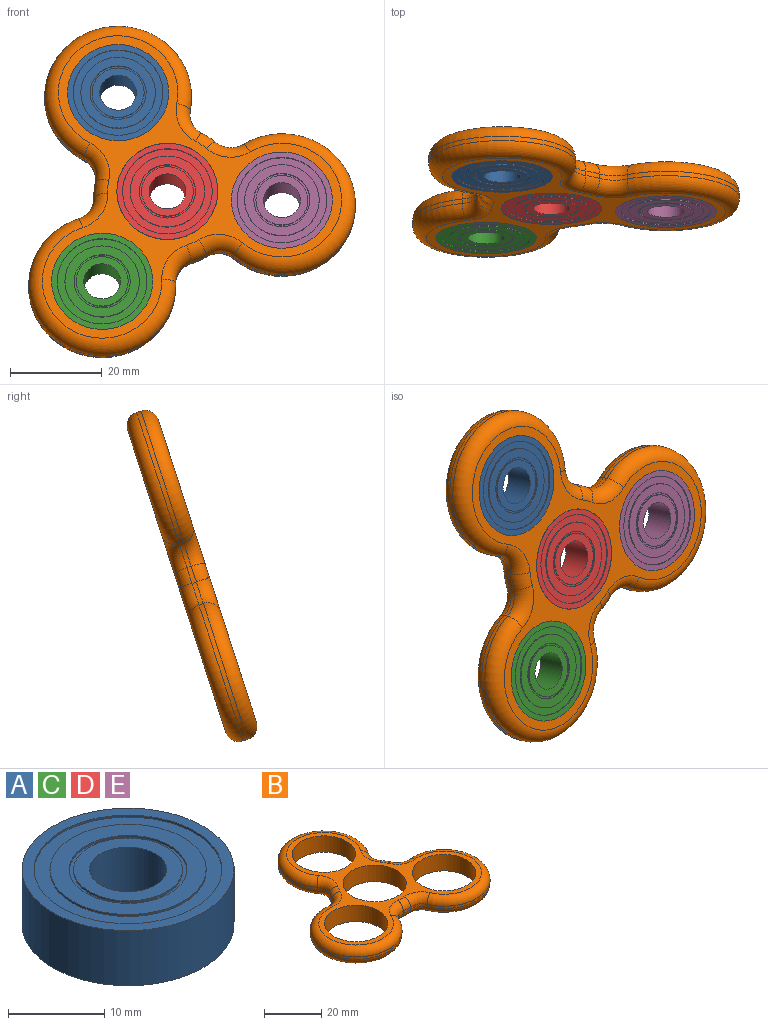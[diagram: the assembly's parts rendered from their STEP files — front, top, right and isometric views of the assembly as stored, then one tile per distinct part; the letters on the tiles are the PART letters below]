
ASSEMBLY  parts=5 mates=4
PART A: 20 faces, bbox 22x22x7 mm
  f0: plane 11.3x11.3mm, normal (0,0,-1), area 50mm2, adj f2,f8
  f1: cylinder r=11mm len=22mm, axis (0,0,-1), area 483.8mm2, adj f3,f12
  f2: cylinder r=4mm len=8mm, axis (0,0,-1), area 175.9mm2, adj f0,f11
  f3: plane 22x22mm, normal (0,0,-1), area 81.5mm2, adj f1,f5
  f4: cylinder r=8.1mm len=16.2mm, axis (0,0,-1), area 12.7mm2, adj f6,f7
  f5: cylinder r=9.75mm len=19.5mm, axis (0,0,-1), area 15.3mm2, adj f3,f6
  f6: plane 19.5x19.5mm, normal (0,0,-1), area 92.5mm2, adj f4,f5
  f7: plane 16.2x16.2mm, normal (0,0,-1), area 89.2mm2, adj f4,f9
  f8: cylinder r=5.65mm len=11.3mm, axis (0,0,-1), area 8.9mm2, adj f0,f10
  f9: cylinder r=6.1mm len=12.2mm, axis (0,0,-1), area 9.6mm2, adj f7,f10
  f10: plane 12.2x12.2mm, normal (0,0,-1), area 16.6mm2, adj f8,f9
  f11: plane 11.3x11.3mm, normal (0,0,1), area 50mm2, adj f2,f17
  f12: plane 22x22mm, normal (0,0,1), area 81.5mm2, adj f1,f14
  f13: cylinder r=8.1mm len=16.2mm, axis (0,0,1), area 12.7mm2, adj f15,f16
  f14: cylinder r=9.75mm len=19.5mm, axis (0,0,1), area 15.3mm2, adj f12,f15
  f15: plane 19.5x19.5mm, normal (0,0,1), area 92.5mm2, adj f13,f14
  f16: plane 16.2x16.2mm, normal (0,0,1), area 89.2mm2, adj f13,f18
  f17: cylinder r=5.65mm len=11.3mm, axis (0,0,1), area 8.9mm2, adj f11,f19
  f18: cylinder r=6.1mm len=12.2mm, axis (0,0,1), area 9.6mm2, adj f16,f19
  f19: plane 12.2x12.2mm, normal (0,0,1), area 16.6mm2, adj f17,f18
PART B: 42 faces, bbox 77.9x72.1x7 mm
  f0: plane 69.3x63.5mm, normal (0,0,-1), area 677.7mm2, adj f4,f6,f9,f11,f18,f19,f20,f21
  f1: cylinder r=16mm len=3.64mm, axis (0,0,-1), area 3.6mm2, adj f12,f15,f21,f34
  f2: cylinder r=16mm len=3.15mm, axis (0,0,-1), area 3.6mm2, adj f13,f16,f29,f33
  f3: cylinder r=16mm len=3.15mm, axis (0,0,-1), area 3.6mm2, adj f14,f17,f22,f41
  f4: cylinder r=11mm len=22mm, axis (0,0,-1), area 483.8mm2, adj f0,f5
  f5: plane 69.3x63.5mm, normal (0,0,1), area 677.7mm2, adj f4,f6,f9,f11,f30,f31,f32,f33
  f6: cylinder r=11mm len=22mm, axis (0,0,-1), area 483.8mm2, adj f0,f5
  f7: cylinder r=16mm len=32mm, axis (0,0,-1), area 70.7mm2, adj f16,f17,f26,f37
  f8: cylinder r=16mm len=32mm, axis (0,0,-1), area 70.7mm2, adj f14,f15,f18,f38
  f9: cylinder r=11mm len=22mm, axis (0,0,-1), area 483.8mm2, adj f0,f5
  f10: cylinder r=16mm len=32mm, axis (0,0,-1), area 70.7mm2, adj f12,f13,f25,f30
  f11: cylinder r=11mm len=22mm, axis (0,0,-1), area 483.8mm2, adj f0,f5
  f12: cylinder r=5mm len=5.16mm, axis (0,0,1), area 6.4mm2, adj f1,f10,f23,f32
  f13: cylinder r=5mm len=5.16mm, axis (0,0,-1), area 6.4mm2, adj f2,f10,f27,f31
  f14: cylinder r=5mm len=5.16mm, axis (0,0,1), area 6.4mm2, adj f3,f8,f20,f40
  f15: cylinder r=5mm len=5.16mm, axis (0,0,-1), area 6.4mm2, adj f1,f8,f19,f36
  f16: cylinder r=5mm len=5.95mm, axis (0,0,1), area 6.4mm2, adj f2,f7,f28,f35
  f17: cylinder r=5mm len=5.95mm, axis (0,0,-1), area 6.4mm2, adj f3,f7,f24,f39
  f18: torus R=13mm, axis (0,0,-1), area 310.3mm2, adj f0,f8,f19,f20
  f19: torus R=8mm, axis (0,0,-1), area 36.6mm2, adj f0,f15,f18,f21
  f20: torus R=8mm, axis (0,0,-1), area 36.6mm2, adj f0,f14,f18,f22
  f21: torus R=13mm, axis (0,0,-1), area 16mm2, adj f0,f1,f19,f23
  f22: torus R=13mm, axis (0,0,-1), area 16mm2, adj f0,f3,f20,f24
  f23: torus R=8mm, axis (0,0,-1), area 36.6mm2, adj f0,f12,f21,f25
  f24: torus R=8mm, axis (0,0,-1), area 36.6mm2, adj f0,f17,f22,f26
  f25: torus R=13mm, axis (0,0,-1), area 310.3mm2, adj f0,f10,f23,f27
  f26: torus R=13mm, axis (0,0,-1), area 310.3mm2, adj f0,f7,f24,f28
  f27: torus R=8mm, axis (0,0,-1), area 36.6mm2, adj f0,f13,f25,f29
  f28: torus R=8mm, axis (0,0,-1), area 36.6mm2, adj f0,f16,f26,f29
  f29: torus R=13mm, axis (0,0,-1), area 16mm2, adj f0,f2,f27,f28
  f30: torus R=13mm, axis (0,0,-1), area 310.3mm2, adj f5,f10,f31,f32
  f31: torus R=8mm, axis (0,0,-1), area 36.6mm2, adj f5,f13,f30,f33
  f32: torus R=8mm, axis (0,0,-1), area 36.6mm2, adj f5,f12,f30,f34
  f33: torus R=13mm, axis (0,0,-1), area 16mm2, adj f2,f5,f31,f35
  f34: torus R=13mm, axis (0,0,-1), area 16mm2, adj f1,f5,f32,f36
  f35: torus R=8mm, axis (0,0,-1), area 36.6mm2, adj f5,f16,f33,f37
  f36: torus R=8mm, axis (0,0,-1), area 36.6mm2, adj f5,f15,f34,f38
  f37: torus R=13mm, axis (0,0,-1), area 310.3mm2, adj f5,f7,f35,f39
  f38: torus R=13mm, axis (0,0,-1), area 310.3mm2, adj f5,f8,f36,f40
  f39: torus R=8mm, axis (0,0,-1), area 36.6mm2, adj f5,f17,f37,f41
  f40: torus R=8mm, axis (0,0,-1), area 36.6mm2, adj f5,f14,f38,f41
  f41: torus R=13mm, axis (0,0,-1), area 16mm2, adj f3,f5,f39,f40
PART C: same geometry as A
PART D: same geometry as A
PART E: same geometry as A
PLACE A rot(axis=(0.93,-0.21,0.29),75.8deg) t=(-9.12,-20.87,16.54)mm
PLACE B rot(axis=(0.93,-0.21,0.29),75.8deg) t=(1.6,-31.17,-3.86)mm
PLACE C rot(axis=(0.93,-0.21,0.29),75.8deg) t=(-12.59,-34.19,-24.52)mm
PLACE D rot(axis=(0.35,-0.55,0.76),128.8deg) t=(1.6,-27.84,-4.94)mm
PLACE E rot(axis=(0.93,-0.21,0.29),75.8deg) t=(26.52,-28.45,-6.85)mm
MATE fastened E.f2 <-> B.f10  axis (0,0.95,-0.31) through (26.52,-31.78,-5.77)mm
MATE fastened B.f1 <-> D.f2  axis (0,0.95,-0.31) through (1.6,-31.17,-3.86)mm
MATE fastened C.f2 <-> B.f8  axis (0,0.95,-0.31) through (-12.59,-37.51,-23.44)mm
MATE fastened A.f2 <-> B.f6  axis (0,0.95,-0.31) through (-9.12,-24.2,17.62)mm
